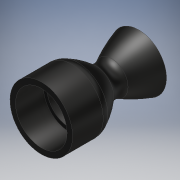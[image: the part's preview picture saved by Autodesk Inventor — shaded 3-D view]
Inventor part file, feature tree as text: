
AUTODESK INVENTOR PART (.ipt)
format: ipt  version: 2017 (Build 210142000, 142)  size: 217,600 bytes
history: native  units: mm
features: fillet x4, revolve x1, move_body x1, sketch x1
ambient origin geometry x8: Origin, YZ Plane, XZ Plane, XY Plane, X Axis, Y Axis, Z Axis, Center Point
bodies: Solid1 (feature_tree)
feature tree (7):
  revolve  "Revolution1"  [1 undecoded]
  move_body  "Move Body1"
  fillet  "Fillet6"  Radius=2.0mm
  fillet  "Fillet7"  Radius=10.0mm
  fillet  "Fillet8"  Radius=34.965555mm
  fillet  "Fillet9"  [1 undecoded]
  sketch  "Sketch1"  dims[d22=90.0deg d26=9.25mm d28=2.0mm d36=10.0mm d37=34.965555mm d38=90.0deg d51=2.0mm d52=5.0mm d53=5.0mm d54=5.0mm d57=36.0mm]
note: 2 required parameter values undecoded (feature->parameter linkage not recoverable at this tier; creation-order binding heuristic only, values carry confidence <= 0.55)